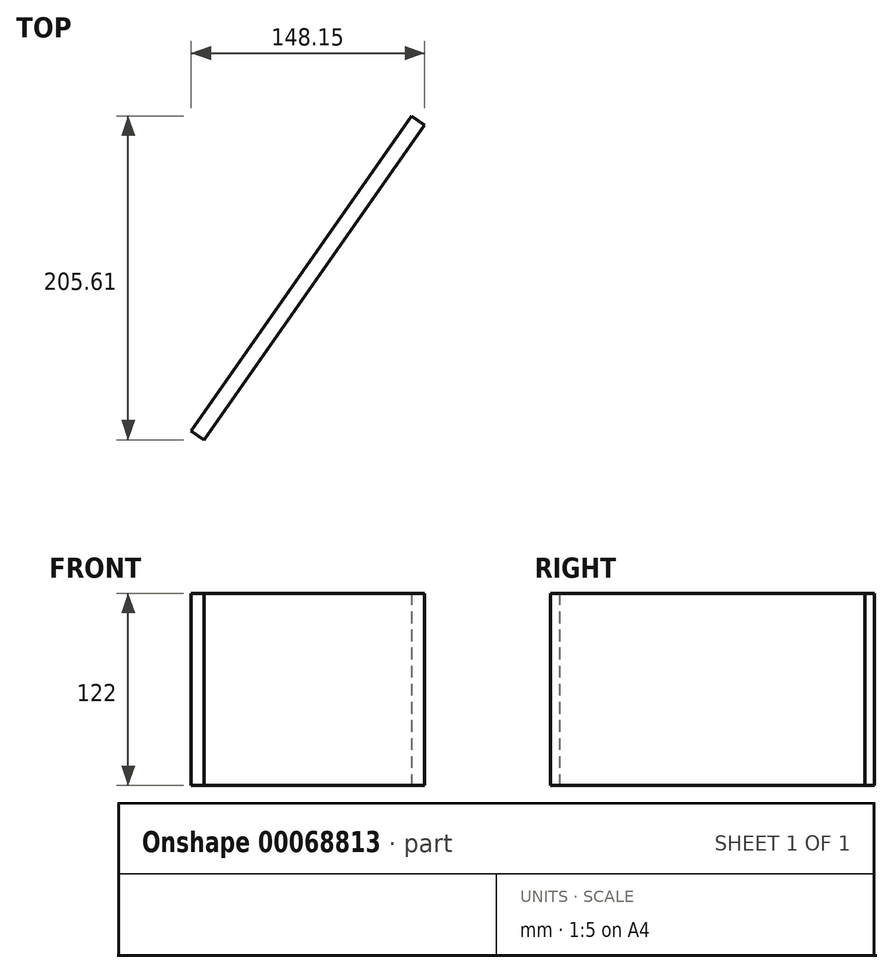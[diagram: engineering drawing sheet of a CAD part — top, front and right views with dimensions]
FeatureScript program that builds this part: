
annotation { "Feature Type Name" : "Feature", "Feature Type Description" : "" }
export const myFeature = defineFeature(function(context is Context, id is Id, definition is map)
    precondition{}
    {
        {
            var Q0;
            Q0=qCreatedBy(makeId("Top.planeOp"),FACE);
            var sketch = newSketch(context, id + "F0", { "sketchPlane" : qUnion([Q0])});
            skLineSegment(sketch, "E0.bottom", {"start": v(-121.66, 43.94) * mm, "end": v(122.34, 43.94) * mm});
            skLineSegment(sketch, "E0.top", {"start": v(-121.66, -78.06) * mm, "end": v(122.34, -78.06) * mm});
            skLineSegment(sketch, "E0.left", {"start": v(-121.66, 43.94) * mm, "end": v(-121.66, -78.06) * mm});
            skLineSegment(sketch, "E0.right", {"start": v(122.34, 43.94) * mm, "end": v(122.34, -78.06) * mm});
            skSolve(sketch);
        }
        {
            var Q0;
            Q0 = qSketchRegion(id + "F0", true);
            extrude(context, id + "F1", {"entities" : qUnion([Q0]), "depth" : 10 * mm});
        }
        {
            var Q0;
            Q0=makeQuery(id+"F1.opExtrude","SWEPT_BODY",BODY,{"disambiguationData":[OSD([sQuery(id+"F0.wireOp",EDGE,"E0.bottom"),sQuery(id+"F0.wireOp",EDGE,"E0.top"),sQuery(id+"F0.wireOp",EDGE,"E0.left"),sQuery(id+"F0.wireOp",EDGE,"E0.right")])]});
            var Q1;
            Q1=makeQuery(id+"F1.opExtrude","CAP_EDGE",EDGE,{"disambiguationData":[OSD([sQuery(id+"F0.wireOp",EDGE,"E0.top")])],"isStart":true});
            transform(context, id + "F2", {"entities" : qUnion([Q0]), "transformType" : TransformType.ROTATION, "transformAxis" : qUnion([Q1]), "angle" : 90 * degree, "makeCopy" : false});
        }
        {
            var Q0;
            Q0=makeQuery(id+"F1.opExtrude","SWEPT_BODY",BODY,{"disambiguationData":[OSD([sQuery(id+"F0.wireOp",EDGE,"E0.bottom"),sQuery(id+"F0.wireOp",EDGE,"E0.top"),sQuery(id+"F0.wireOp",EDGE,"E0.left"),sQuery(id+"F0.wireOp",EDGE,"E0.right")])]});
            var Q1;
            Q1=makeQuery(id+"F1.opExtrude","CAP_EDGE",EDGE,{"disambiguationData":[OSD([sQuery(id+"F0.wireOp",EDGE,"E0.left")])],"isStart":false});
            transform(context, id + "F3", {"entities" : qUnion([Q0]), "transformType" : TransformType.ROTATION, "transformAxis" : qUnion([Q1]), "angle" : 125 * degree, "makeCopy" : false});
        }
    });
